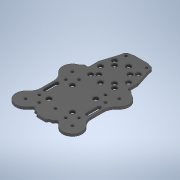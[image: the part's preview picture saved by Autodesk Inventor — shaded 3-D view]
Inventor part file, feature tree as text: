
AUTODESK INVENTOR PART (.ipt)
format: ipt  version: 2020 (Build 240168000, 168)  size: 477,184 bytes
history: native  units: in
note: dims shown in document units (in); Inventor stores cm internally (conversion verified against a paired STEP export)
features: sketch x5, extrude x3, projected_geometry x3
ambient origin geometry x8: Origin, YZ Plane, XZ Plane, XY Plane, X Axis, Y Axis, Z Axis, Center Point
bodies: Solid2 (feature_tree), Solid1 (feature_tree)
feature tree (11):
  extrude  "Extrusion1"  Depth=0.2362in
  sketch  "Sketch3"  dims[d3=0.2362in d4=0.2362in]
  sketch  "Sketch4"  dims[d5=0.2362in d6=0.2362in]
  extrude  "Extrusion2"  Depth=0.2362in
  extrude  "Extrusion3"  Depth=0.2362in
  sketch  "Sketch2"  dims[d1=0.2362in d2=0.2362in]
  projected_geometry  "Projected Loop2"
  projected_geometry  "Projected Loop3"
  projected_geometry  "Projected Loop4"
  sketch  "Sketch5"  dims[d7=0.2362in]
  sketch  "Sketch6"  dims[d8=0.2362in d9=0.2362in d10=0.2362in d11=0.2362in d12=0.2362in d13=0.3937in d14=0.0in d27=0.3937in d28=0.0in d29=0.2362in d30=0.2362in d31=0.2362in d32=0.2362in d33=0.2362in d34=1.0039in d35=1.0039in d36=1.0039in d37=1.0039in d38=1.4197in d39=0.3937in d40=0.0in]
